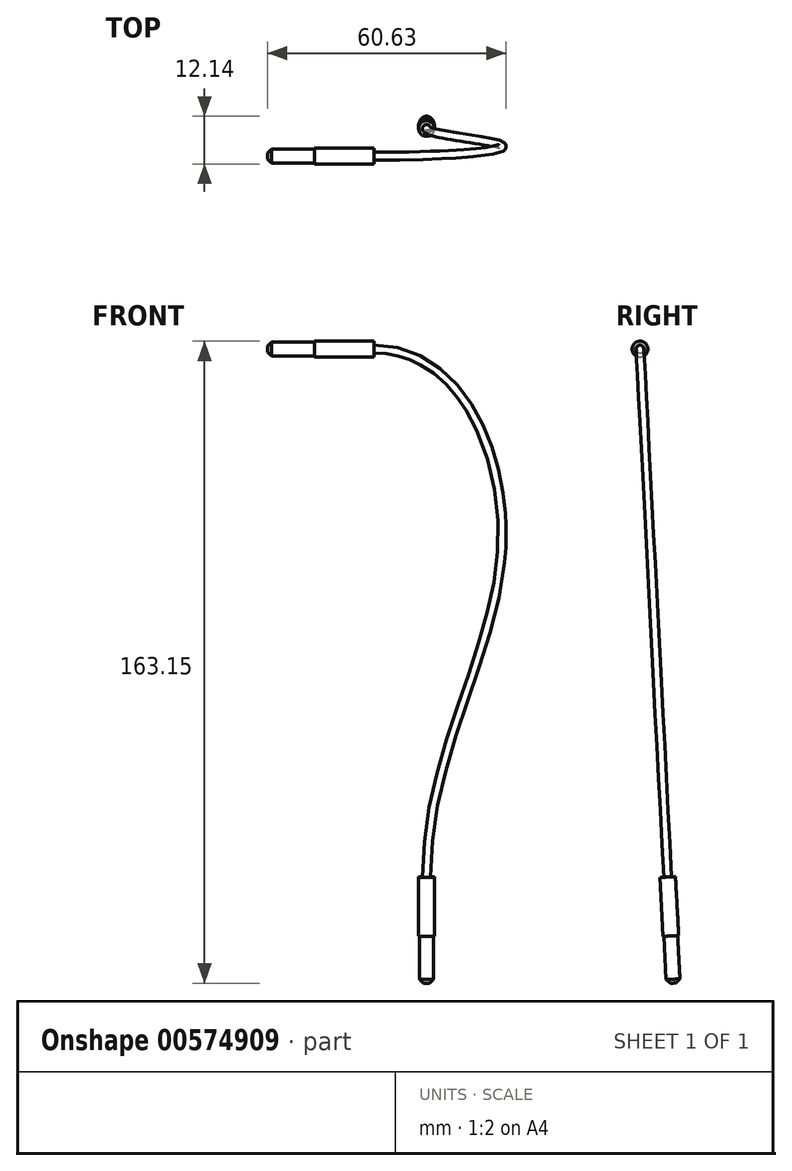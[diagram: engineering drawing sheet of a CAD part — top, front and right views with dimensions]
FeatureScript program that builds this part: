
annotation { "Feature Type Name" : "Feature", "Feature Type Description" : "" }
export const myFeature = defineFeature(function(context is Context, id is Id, definition is map)
    precondition{}
    {
        {
            var Q0;
            Q0=qCreatedBy(makeId("Front.planeOp"),FACE);
            var sketch = newSketch(context, id + "F0", { "sketchPlane" : qUnion([Q0])});
            skLineSegment(sketch, "E0.0", {"start": v(0, 0) * mm, "end": v(22.45, 0) * mm, "construction": true});
            skSolve(sketch);
        }
        {
            var Q0;
            Q0=sQuery(id+"F0.wireOp",EDGE,"E0.0");
            cPlane(context, id + "F1", {"entities" : qUnion([Q0]), "cplaneType" : CPlaneType.LINE_ANGLE, "offset" : 25 * mm, "angle" : 3 * degree, "width" : 150 * mm, "height" : 150 * mm});
        }
        {
            var Q0;
            Q0=qCreatedBy(id+"F1.planeOp",FACE);
            var sketch = newSketch(context, id + "F2", { "sketchPlane" : qUnion([Q0])});
            skFitSpline(sketch, "E1", {"points": [v(0, 0) * mm, v(-32.6, -48.57) * mm, v(-13.4, -134.33) * mm], "startDerivative": vector(-145.36, 0) * mm, "endDerivative": vector(0, -181) * mm});
            skLineSegment(sketch, "E2", {"start": v(0, 0) * mm, "end": v(22.45, 0) * mm, "construction": true});
            skLineSegment(sketch, "E3", {"start": v(-13.4, -134.33) * mm, "end": v(-13.4, -173.21) * mm, "construction": true});
            skSolve(sketch);
        }
        {
            var Q0;
            Q0=qCreatedBy(makeId("Right.planeOp"),FACE);
            var sketch = newSketch(context, id + "F3", { "sketchPlane" : qUnion([Q0])});
            skCircle(sketch, "E4", {"center": v(0, 0) * mm, "radius": 1 * mm});
            skSolve(sketch);
        }
        {
            var Q0;
            Q0=makeQuery(id+"F3.imprint","IMPRINT",FACE,{"disambiguationData":[TD([[makeQuery(id+"F3.imprint","IMPRINT",EDGE,{"derivedFrom":sQuery(id+"F3.wireOp",EDGE,"E4")}),1.0]])]});
            var Q1;
            Q1=sQuery(id+"F2.wireOp",EDGE,"E1");
            sweep(context, id + "F4", {"profiles" : qUnion([Q0]), "path" : qUnion([Q1])});
        }
        {
            var Q0;
            Q0=qCreatedBy(makeId("Right.planeOp"),FACE);
            var sketch = newSketch(context, id + "F5", { "sketchPlane" : qUnion([Q0])});
            skCircle(sketch, "E5", {"center": v(0, 0) * mm, "radius": 2 * mm});
            skSolve(sketch);
        }
        {
            var Q0;
            Q0=makeQuery(id+"F5.imprint","IMPRINT",FACE,{"disambiguationData":[TD([[makeQuery(id+"F5.imprint","IMPRINT",EDGE,{"derivedFrom":sQuery(id+"F5.wireOp",EDGE,"E5")}),1.0]])]});
            extrude(context, id + "F6", {"entities" : qUnion([Q0]), "operationType" : NewBodyOperationType.ADD, "oppositeDirection" : true, "depth" : 15 * mm, "offsetDistance" : 25 * mm});
        }
        {
            var Q0;
            Q0=makeQuery(id+"F4.opSweep","CAP_FACE",FACE,{"disambiguationData":[OSD([sQuery(id+"F2.wireOp",VERTEX,"E1.end"),sQuery(id+"F3.wireOp",EDGE,"E4")])],"isStart":false});
            var sketch = newSketch(context, id + "F7", { "sketchPlane" : qUnion([Q0])});
            skCircle(sketch, "E6", {"center": v(13.4, 0) * mm, "radius": 2 * mm});
            skSolve(sketch);
        }
        {
            var Q0;
            Q0 = qSketchRegion(id + "F7", true);
            extrude(context, id + "F8", {"entities" : qUnion([Q0]), "operationType" : NewBodyOperationType.ADD, "depth" : 15 * mm, "offsetDistance" : 25 * mm});
        }
        {
            var Q0;
            Q0=makeQuery(id+"F8.opExtrude","CAP_FACE",FACE,{"disambiguationData":[OSD([sQuery(id+"F7.wireOp",EDGE,"E6")])],"isStart":false});
            var sketch = newSketch(context, id + "F9", { "sketchPlane" : qUnion([Q0])});
            skCircle(sketch, "E7", {"center": v(13.4, 0) * mm, "radius": 1.75 * mm});
            skSolve(sketch);
        }
        {
            var Q0;
            Q0 = qSketchRegion(id + "F9", true);
            extrude(context, id + "F10", {"entities" : qUnion([Q0]), "depth" : 12 * mm, "offsetDistance" : 25 * mm});
        }
        {
            var Q0;
            Q0=makeQuery(id+"F10.opExtrude","CAP_EDGE",EDGE,{"disambiguationData":[OSD([sQuery(id+"F9.wireOp",EDGE,"E7")])],"isStart":false});
            chamfer(context, id + "F11", {"entities" : qUnion([Q0]), "width" : 1 * mm, "tangentPropagation" : true});
        }
        {
            var Q0;
            Q0=makeQuery(id+"F6.opExtrude","CAP_FACE",FACE,{"disambiguationData":[OSD([sQuery(id+"F5.wireOp",EDGE,"E5")])],"isStart":false});
            var sketch = newSketch(context, id + "F12", { "sketchPlane" : qUnion([Q0])});
            skCircle(sketch, "E8", {"center": v(0, 0) * mm, "radius": 1.75 * mm});
            skSolve(sketch);
        }
        {
            var Q0;
            Q0=makeQuery(id+"F12.imprint","IMPRINT",FACE,{"disambiguationData":[TD([[makeQuery(id+"F12.imprint","IMPRINT",EDGE,{"derivedFrom":sQuery(id+"F12.wireOp",EDGE,"E8")}),1.0]])]});
            extrude(context, id + "F13", {"entities" : qUnion([Q0]), "depth" : 12 * mm, "offsetDistance" : 25 * mm});
        }
        {
            var Q0;
            Q0=makeQuery(id+"F13.opExtrude","CAP_EDGE",EDGE,{"disambiguationData":[OSD([sQuery(id+"F12.wireOp",EDGE,"E8")])],"isStart":false});
            chamfer(context, id + "F14", {"entities" : qUnion([Q0]), "width" : 1 * mm, "tangentPropagation" : true});
        }
    });
